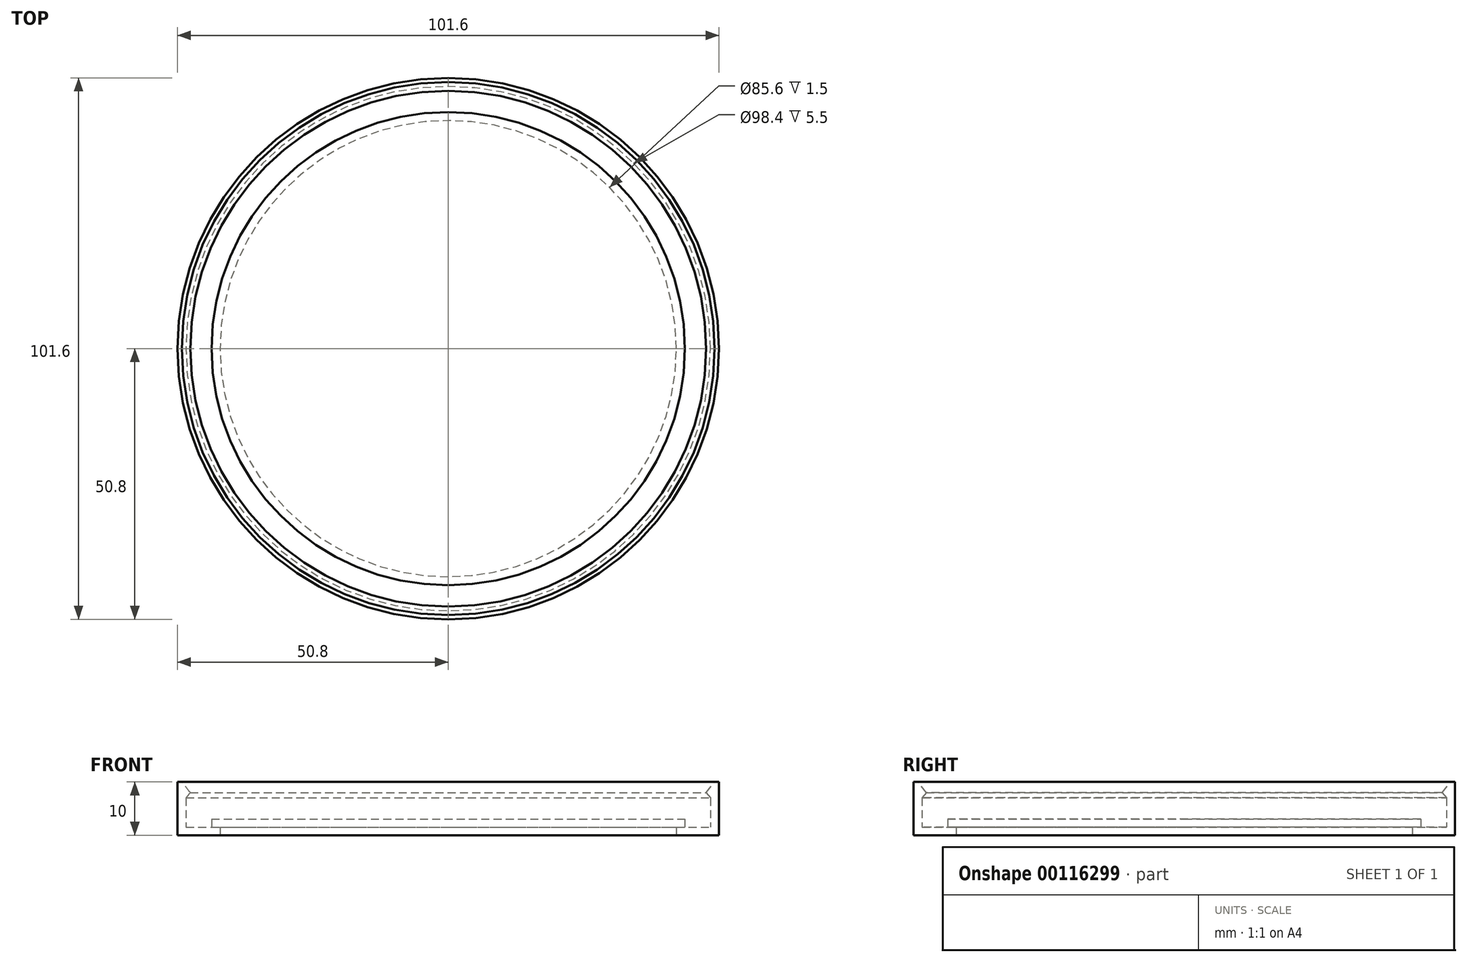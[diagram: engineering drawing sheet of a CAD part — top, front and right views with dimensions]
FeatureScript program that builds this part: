
annotation { "Feature Type Name" : "Feature", "Feature Type Description" : "" }
export const myFeature = defineFeature(function(context is Context, id is Id, definition is map)
    precondition{}
    {
        {
            var Q0;
            Q0=qCreatedBy(makeId("Front.planeOp"),FACE);
            var sketch = newSketch(context, id + "F0", { "sketchPlane" : qUnion([Q0])});
            skLineSegment(sketch, "E0", {"start": v(0, 3) * mm, "end": v(-44.4, 3) * mm});
            skLineSegment(sketch, "E1", {"start": v(-44.4, 3) * mm, "end": v(-44.4, 1.5) * mm});
            skLineSegment(sketch, "E2", {"start": v(-44.4, 1.5) * mm, "end": v(-49.2, 1.5) * mm});
            skLineSegment(sketch, "E3", {"start": v(-48.4, 8) * mm, "end": v(-50, 10) * mm});
            skLineSegment(sketch, "E4", {"start": v(-50, 10) * mm, "end": v(-50.8, 10) * mm});
            skLineSegment(sketch, "E5", {"start": v(-50.8, 10) * mm, "end": v(-50.8, 0) * mm});
            skLineSegment(sketch, "E6", {"start": v(-50.8, 0) * mm, "end": v(-42.8, 0) * mm});
            skLineSegment(sketch, "E7", {"start": v(-42.8, 0) * mm, "end": v(-42.8, 1.5) * mm});
            skLineSegment(sketch, "E8", {"start": v(-42.8, 1.5) * mm, "end": v(0, 1.5) * mm});
            skLineSegment(sketch, "E9", {"start": v(0, 1.5) * mm, "end": v(0, 3) * mm});
            skLineSegment(sketch, "E10", {"start": v(-48.4, 8) * mm, "end": v(-49.2, 7) * mm});
            skLineSegment(sketch, "E11", {"start": v(-49.2, 7) * mm, "end": v(-49.2, 1.5) * mm});
            skSolve(sketch);
        }
        {
            var Q0;
            Q0=makeQuery(id+"F0.imprint","IMPRINT",FACE,{"disambiguationData":[TD([[makeQuery(id+"F0.imprint","IMPRINT",EDGE,{"derivedFrom":sQuery(id+"F0.wireOp",EDGE,"E0")}),1.0]])]});
            var Q1;
            Q1=sQuery(id+"F0.wireOp",EDGE,"E9");
            revolve(context, id + "F1", {"entities" : qUnion([Q0]), "axis" : qUnion([Q1]), "revolveType" : RevolveType.FULL});
        }
    });
